# Revit family: Gira_000830
name_source: partatom
category: Electrical Fixtures
revit_build: Autodesk Revit 2017 (Build: 20160225_1515(x64)
units: mm (PartAtom-declared; Revit-internal decimal feet)

## family parameters
Always vertical = Yes
Cut with Voids When Loaded = No
Maintain Annotation Orientation = No
Part Type = Normal
Room Calculation Point = No
Round Connector Dimension = Use Diameter
Shared = No
Work Plane-Based = No

## types (1)
- Adapter cab.entry 1-g channel 15 x 15 mm WP SM grey
    BIM = https://media.live.bim.site
    BIMSITE_PRODUCT_ID = ace2d32275819c874db17f32754eef9128f813aa
    Colour = Grey
    Cost = 0 $
    Description = Adap.cab.entry 1g chan.15x15 WP SM GY Adapter for cable entry, 1-gang for duct 15 x 15 mm grey
    GTIN = 4010337008309
    HAN = 000830
    HeinzeBIM = https://www.heinze.de
    Manufacturer = Gira
    Model = Duct slider
    Suitable for built-up box flush-mounted switching equipment = Yes
    URL = https://www.gira.de

## geometry (parser evidence)
native form markers: Blend x2, Sweep x4
no freeform markers — native parametric forms only
